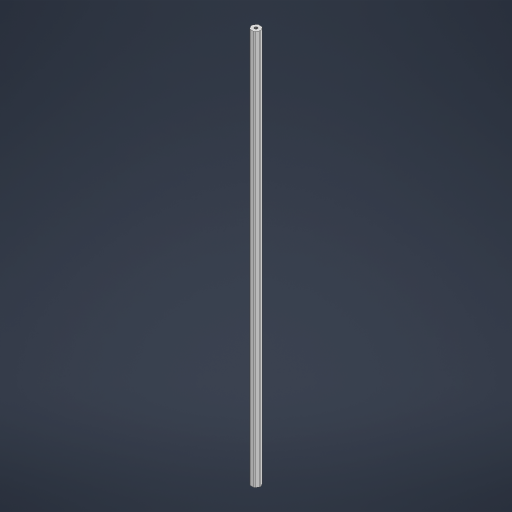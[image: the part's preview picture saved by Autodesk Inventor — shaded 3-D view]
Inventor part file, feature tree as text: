
AUTODESK INVENTOR PART (.ipt)
format: ipt  version: 2023 (Build 270158000, 158)  size: 755,200 bytes
history: native  units: in
note: dims shown in document units (in); Inventor stores cm internally (conversion verified against a paired STEP export)
features: mirror x1
ambient origin geometry x8: Origin, YZ Plane, XZ Plane, XY Plane, X Axis, Y Axis, Z Axis, Center Point
bodies: Solid1 (feature_tree)
feature tree (1):
  mirror  "Mirror2"
